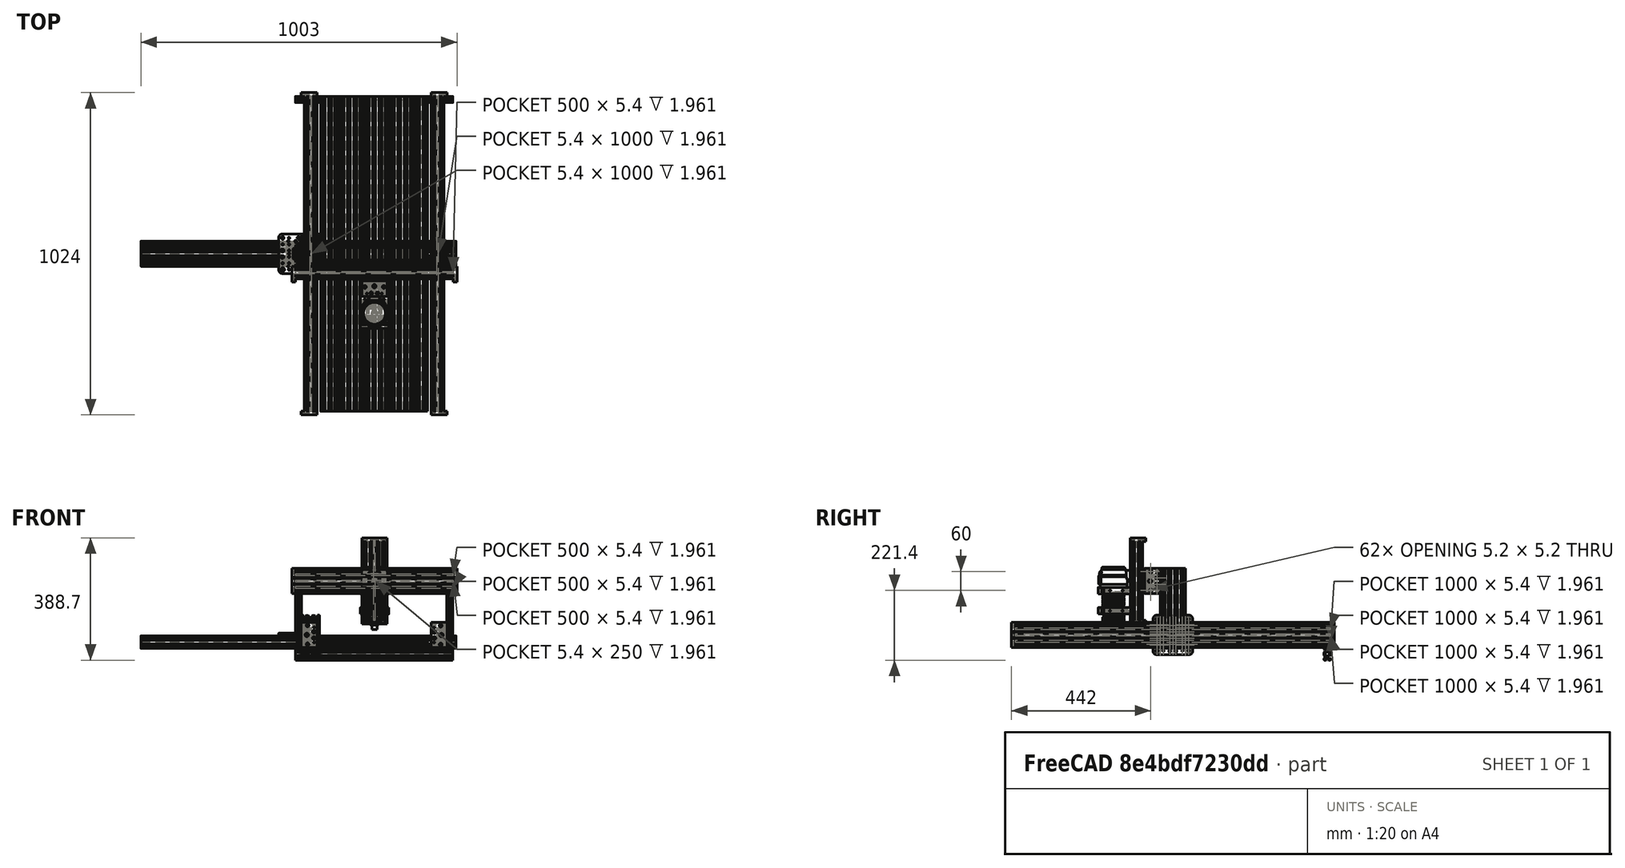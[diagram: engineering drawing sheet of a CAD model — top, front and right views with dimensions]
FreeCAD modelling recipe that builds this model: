
FCSTD DOCUMENT  (FreeCAD 0.19R24276 (Git))
Label: cnc
License: All rights reserved
LicenseURL: http://en.wikipedia.org/wiki/All_rights_reserved
objects: Part::Feature×44, PartDesign::FeatureBase×17, PartDesign::Body×17, Part::MultiFuse×7, App::DocumentObjectGroup×7, Part::Refine×1
note: 86 computed .brp shape members not serialized (recipe doc carries the construction recipe); baked Part::Feature solids carry a one-line shape summary decoded from their .brp

FEATURE [Part::Feature] Part__Feature011  label="Router Spindle Mount"
  Placement = pos=(241,-189,131) rot=(1,0,0;1.5708rad)
  shape: bbox 90.8 x 102.7 x 20 mm, 224 faces, 2 solids (baked)
FEATURE [Part::Feature] Part__Feature012  label="Dewalt DWP611"
  Placement = pos=(241,-189,38) rot=(1,0,0;1.5708rad)
  shape: bbox 86.67 x 107.5 x 199.1 mm, 229 faces (baked)
FEATURE [Part::Feature] Part__Feature013  label="Router Spindle Mount001"
  Placement = pos=(241,-189,66.8) rot=(1,0,0;1.5708rad)
  shape: bbox 90.8 x 102.7 x 20 mm, 224 faces, 2 solids (baked)
FEATURE [Part::Feature] Part__Feature014  label="Frame Front"
  Placement = pos=(-10,-490,-60) rot=(0.57735,0.57735,0.57735;2.0944rad)
  shape: bbox 500 x 20 x 40 mm, 116 faces (baked)
FEATURE [Part::Feature] Part__Feature015  label="V-Slot 20x80x1000 Linear Rail"
  Placement = pos=(250,500,-30) rot=(0.57735,-0.57735,0.57735;2.0944rad)
  shape: bbox 80 x 1000 x 20 mm, 204 faces (baked)
FEATURE [Part::Feature] Part__Feature016  label="V-Slot 20x80x1000 Linear Rail001"
  Placement = pos=(170,500,-30) rot=(0.57735,-0.57735,0.57735;2.0944rad)
  shape: bbox 80 x 1000 x 20 mm, 204 faces (baked)
FEATURE [Part::Feature] Part__Feature017  label="V-Slot 20x80x1000 Linear Rail002"
  Placement = pos=(330,500,-30) rot=(0.57735,-0.57735,0.57735;2.0944rad)
  shape: bbox 80 x 1000 x 20 mm, 204 faces (baked)
FEATURE [Part::Feature] Part__Feature020  label="V-Slot 20x40x1000 Linear Rail"
  Placement = pos=(390,-500,-30) rot=(0.57735,-0.57735,-0.57735;4.18879rad)
  shape: bbox 40 x 1000 x 20 mm, 116 faces (baked)
FEATURE [Part::Feature] Part__Feature021  label="V-Slot 20x60x1000 Linear Rail"
  Placement = pos=(100,500,-30) rot=(0.57735,-0.57735,0.57735;2.0944rad)
  shape: bbox 60 x 1000 x 20 mm, 160 faces (baked)
FEATURE [Part::Refine] Part__Feature014001  label="Frame Back"
  Placement = pos=(0,980,0) rot=(0,0,1;0rad)
  Source = -> Part__Feature014
FEATURE [Part::Feature] Part__Feature014003  label="Xtreme Mini V Wheel"
  shape: bbox 8.8 x 15.23 x 15.23 mm, 16 faces (baked)
FEATURE [Part::Feature] Part__Feature014004  label="Ball Bearing 5 x 10 x 4.2"
  Placement = pos=(2.6,0,0) rot=(0,0,1;0rad)
  shape: bbox 4.2 x 10 x 10 mm, 18 faces (baked)
FEATURE [Part::Feature] Part__Feature014006  label="Precision Shim 8 x 5 x 1"
  Placement = pos=(5.7,0,0) rot=(0,0,1;1.5708rad)
  shape: bbox 1 x 8 x 8 mm, 6 faces (baked)
FEATURE [Part::Feature] Part__Feature014007  label="Ball Bearing 5 x 10 x 4.004"
  Placement = pos=(-2.6,0,0) rot=(0,0,1;0rad)
  shape: bbox 4.2 x 10 x 10 mm, 18 faces (baked)
FEATURE [Part::Feature] Part__Feature014008  label="Precision Shim 8 x 5 x 002"
  Placement = pos=(-4.7,0,0) rot=(0,0,1;1.5708rad)
  shape: bbox 1 x 8 x 8 mm, 6 faces (baked)
FEATURE [Part::Feature] Part__Feature014009  label="Aluminum Spacer 6mm"
  Placement = pos=(5.7,0,0) rot=(0,1,0;1.5708rad)
  shape: bbox 6 x 10 x 10 mm, 14 faces (baked)
FEATURE [Part::MultiFuse] Fusion001003  label="Wheel"
  Shapes = -> [Part__Feature014003,Part__Feature014009,Part__Feature014008,Part__Feature014007,Part__Feature014006,Part__Feature014004]
FEATURE [Part::Feature] Part__Feature014010  label="C-Beam Gantry Plate"
  shape: bbox 77.15 x 6 x 77.15 mm, 93 faces (baked)
FEATURE [PartDesign::FeatureBase] Clone
  BaseFeature = -> Fusion001003
FEATURE [PartDesign::Body] Body  label="Wheel1"
  BaseFeature = -> Fusion001003
  Group = -> [Clone]
  Origin = -> Origin
  Placement = pos=(-30,-11.7,14.25) rot=(0,0,1;1.5708rad)
  Tip = -> Clone
FEATURE [PartDesign::FeatureBase] Clone001
  BaseFeature = -> Fusion001003
FEATURE [PartDesign::Body] Body001  label="Wheel2"
  BaseFeature = -> Fusion001003
  Group = -> [Clone001]
  Origin = -> Origin001
  Placement = pos=(30,-11.7,14.25) rot=(0,0,1;1.5708rad)
  Tip = -> Clone001
FEATURE [PartDesign::FeatureBase] Clone002
  BaseFeature = -> Fusion001003
FEATURE [PartDesign::Body] Body002  label="Wheel3"
  BaseFeature = -> Fusion001003
  Group = -> [Clone002]
  Origin = -> Origin002
  Placement = pos=(30,-11.7,-14.25) rot=(0,0,1;1.5708rad)
  Tip = -> Clone002
FEATURE [PartDesign::FeatureBase] Clone003
  BaseFeature = -> Fusion001003
FEATURE [PartDesign::Body] Body003  label="Wheel4"
  BaseFeature = -> Fusion001003
  Group = -> [Clone003]
  Origin = -> Origin003
  Placement = pos=(-30,-11.7,-14.25) rot=(0,0,1;1.5708rad)
  Tip = -> Clone003
FEATURE [Part::MultiFuse] Fusion001004  label="Granty Plate"
  Shapes = -> [Part__Feature014010,Body,Body001,Body002,Body003]
FEATURE [Part::Feature] Part__Feature003001  label="C-Beam 40x80x1000 Linear Rail002"
  Placement = pos=(37.7,500,0.3) rot=(0,0.707107,-0.707107;3.14159rad)
  shape: bbox 40 x 1000 x 80 mm, 294 faces (baked)
FEATURE [Part::Feature] Part__Feature014011  label="C-Beam End Mount1"
  Placement = pos=(57.7,-500,-39.7) rot=(0.57735,-0.57735,0.57735;2.0944rad)
  shape: bbox 50 x 12 x 80 mm, 43 faces (baked)
FEATURE [Part::Feature] Part__Feature014011001  label="C-Beam End Mount2"
  Placement = pos=(57.7,500,40.3) rot=(0.57735,-0.57735,-0.57735;4.18879rad)
  shape: bbox 50 x 12 x 80 mm, 43 faces (baked)
FEATURE [Part::Feature] Part__Feature002001  label="C-Beam 40x80x500 Linear Rail001"
  Placement = pos=(-250,0,0.3) rot=(0.57735,0.57735,0.57735;2.0944rad)
  shape: bbox 500 x 40 x 80 mm, 294 faces (baked)
FEATURE [PartDesign::FeatureBase] Clone008
  BaseFeature = -> Fusion001004
FEATURE [PartDesign::Body] Body008
  BaseFeature = -> Fusion001004
  Group = -> [Clone008]
  Origin = -> Origin008
  Placement = pos=(0,21.7,0) rot=(0,0,1;0rad)
  Tip = -> Clone008
FEATURE [Part::Feature] Part__Feature014011002  label="C-Beam End Mount003"
  Placement = pos=(-250,-20,-39.7) rot=(0,-1,0;1.5708rad)
  shape: bbox 12 x 50 x 80 mm, 43 faces (baked)
FEATURE [Part::Feature] Part__Feature014011002001  label="C-Beam End Mount004"
  Placement = pos=(250,-20,40.3) rot=(0,1,0;1.5708rad)
  shape: bbox 12 x 50 x 80 mm, 43 faces (baked)
FEATURE [Part::MultiFuse] Fusion001006  label="C-Beam 500 Linear Rail"
  Shapes = -> [Part__Feature002001,Body008,Part__Feature014011002,Part__Feature014011002001]
FEATURE [PartDesign::FeatureBase] Clone009
  BaseFeature = -> Fusion001006
FEATURE [PartDesign::Body] Body009  label="x-rail"
  BaseFeature = -> Fusion001006
  Group = -> [Clone009]
  Origin = -> Origin009
  Placement = pos=(241,-60,171.7) rot=(1,0,0;3.14159rad)
  Tip = -> Clone009
FEATURE [App::DocumentObjectGroup] Group003  label="x-axis"
  Group = -> [Body009]
FEATURE [Part::Feature] Part__Feature014011002002  label="C-Beam 40x80x250 Linear Rail001"
  Placement = pos=(0,125,0.3) rot=(0,0.707107,-0.707107;3.14159rad)
  shape: bbox 40 x 250 x 80 mm, 294 faces (baked)
FEATURE [PartDesign::FeatureBase] Clone010
  BaseFeature = -> Fusion001004
FEATURE [PartDesign::Body] Body010
  BaseFeature = -> Fusion001004
  Group = -> [Clone010]
  Origin = -> Origin010
  Placement = pos=(-21.7,0,0) rot=(0,0,1;1.5708rad)
  Tip = -> Clone010
FEATURE [Part::Feature] Part__Feature014011002003  label="C-Beam End Mount005"
  Placement = pos=(20,-125,-39.7) rot=(0.57735,-0.57735,0.57735;2.0944rad)
  shape: bbox 50 x 12 x 80 mm, 43 faces (baked)
FEATURE [Part::Feature] Part__Feature014011001001  label="C-Beam End Mount006"
  Placement = pos=(20,125,40.3) rot=(0.57735,-0.57735,-0.57735;4.18879rad)
  shape: bbox 50 x 12 x 80 mm, 43 faces (baked)
FEATURE [Part::MultiFuse] Fusion  label="C-Beam 250 Linear Rail"
  Shapes = -> [Body010,Part__Feature014011002003,Part__Feature014011001001,Part__Feature014011002002]
FEATURE [PartDesign::FeatureBase] Clone011
  BaseFeature = -> Fusion
FEATURE [PartDesign::Body] Body011  label="z-rail"
  BaseFeature = -> Fusion
  Group = -> [Clone011]
  Origin = -> Origin011
  Placement = pos=(241,-115.4,171.7) rot=(0.57735,-0.57735,-0.57735;2.0944rad)
  Tip = -> Clone011
FEATURE [Part::Feature] Part__Feature  label="y-left"
  Placement = pos=(0,0,-38.6) rot=(0,0,1;0rad)
  shape: bbox 20 x 80 x 250 mm, 200 faces (baked)
FEATURE [Part::Feature] Part__Feature001  label="y-right"
  Placement = pos=(480,0,-38.6) rot=(0,0,1;0rad)
  shape: bbox 20 x 80 x 250 mm, 200 faces (baked)
FEATURE [App::DocumentObjectGroup] Group  label="Frame"
  Group = -> [Part__Feature014,Part__Feature014001]
FEATURE [App::DocumentObjectGroup] Group009  label="z-axis"
  Group = -> [Part__Feature012,Body011,Part__Feature011,Part__Feature013]
FEATURE [App::DocumentObjectGroup] Group010  label="Bed"
  Group = -> [Part__Feature020,Part__Feature016,Part__Feature017,Part__Feature021,Part__Feature015]
FEATURE [Part::Feature] Part__Feature014011002004  label="Solid V Wheel"
  shape: bbox 10.2 x 23.9 x 23.9 mm, 16 faces (baked)
FEATURE [Part::Feature] Part__Feature014011002005  label="Ball Bearing 8 x 16 x 5"
  Placement = pos=(-3,0,0) rot=(0,0,1;0rad)
  shape: bbox 5 x 16 x 16 mm, 18 faces (baked)
FEATURE [Part::Feature] Part__Feature014011002006  label="Ball Bearing 8 x 16 x 006"
  Placement = pos=(3,0,0) rot=(0,0,1;0rad)
  shape: bbox 5 x 16 x 16 mm, 18 faces (baked)
FEATURE [Part::Feature] Part__Feature014011002007  label="Precision Shim 8 x 5 x 003"
  Placement = pos=(0.5,0,0) rot=(0,0,1;1.5708rad)
  shape: bbox 1 x 8 x 8 mm, 6 faces (baked)
FEATURE [Part::Feature] Part__Feature014011002008  label="Precision Shim 8 x 5 x 004"
  Placement = pos=(-5.5,0,0) rot=(0,0,1;1.5708rad)
  shape: bbox 1 x 8 x 8 mm, 6 faces (baked)
FEATURE [Part::Feature] Part__Feature014011002009  label="Aluminum Spacer 6mm001"
  Placement = pos=(-12.5,0,0) rot=(0,1,0;1.5708rad)
  shape: bbox 6 x 10 x 10 mm, 14 faces (baked)
FEATURE [Part::Feature] Part__Feature014011002010  label="C-Beam Gantry Plate XLarge"
  shape: bbox 125 x 125 x 6 mm, 167 faces (baked)
FEATURE [Part::Feature] Part__Feature014011002011  label="C-Beam 40x80x1000 Linear Rail"
  Placement = pos=(500,0,-22.5) rot=(0,-1,0;1.5708rad)
  shape: bbox 1000 x 80 x 40 mm, 294 faces (baked)
FEATURE [Part::Feature] Part__Feature014011002015  label="Ball Bearing 8 x 16 x 007"
  Placement = pos=(17,0,0) rot=(0,0,1;0rad)
  shape: bbox 5 x 16 x 16 mm, 18 faces (baked)
FEATURE [Part::Feature] Part__Feature014011002016  label="Precision Shim 8 x 5 x 007"
  Placement = pos=(20.5,0,0) rot=(0,0,1;1.5708rad)
  shape: bbox 1 x 8 x 8 mm, 6 faces (baked)
FEATURE [Part::Feature] Part__Feature014011002017  label="Ball Bearing 8 x 16 x 008"
  Placement = pos=(23,0,0) rot=(0,0,1;0rad)
  shape: bbox 5 x 16 x 16 mm, 18 faces (baked)
FEATURE [Part::Feature] Part__Feature014011002018  label="Solid V Wheel001"
  Placement = pos=(20,0,0) rot=(0,0,1;0rad)
  shape: bbox 10.2 x 23.9 x 23.9 mm, 16 faces (baked)
FEATURE [Part::Feature] Part__Feature014011002019  label="Aluminum Spacer 9mm"
  Placement = pos=(5.5,0,0) rot=(0,1,0;1.5708rad)
  shape: bbox 9 x 10 x 10 mm, 14 faces (baked)
FEATURE [Part::Feature] Part__Feature014011002020  label="Precision Shim 8 x 5 x 008"
  Placement = pos=(26.5,0,0) rot=(0,0,1;1.5708rad)
  shape: bbox 1 x 8 x 8 mm, 6 faces (baked)
FEATURE [Part::Feature] Part__Feature014011002021  label="Aluminum Spacer 6mm002"
  Placement = pos=(32.5,0,0) rot=(0.707107,0,-0.707107;3.14159rad)
  shape: bbox 6 x 10 x 10 mm, 14 faces (baked)
FEATURE [Part::MultiFuse] Fusion001007  label="Double Wheel"
  Shapes = -> [Part__Feature014011002004,Part__Feature014011002005,Part__Feature014011002006,Part__Feature014011002007,Part__Feature014011002008,Part__Feature014011002009,Part__Feature014011002015,Part__Feature014011002016,Part__Feature014011002017,Part__Feature014011002018,Part__Feature014011002019,Part__Feature014011002020,Part__Feature014011002021]
FEATURE [Part::Feature] Part__Feature014011002022  label="C-Beam Gantry Plate XLarge001"
  shape: bbox 125 x 125 x 6 mm, 167 faces (baked)
FEATURE [PartDesign::FeatureBase] Clone012
  BaseFeature = -> Fusion001007
FEATURE [PartDesign::Body] Body012
  BaseFeature = -> Fusion001007
  Group = -> [Clone012]
  Origin = -> Origin012
  Placement = pos=(50.32,-50.3,-12.5) rot=(0,1,0;1.5708rad)
  Tip = -> Clone012
FEATURE [PartDesign::FeatureBase] Clone013
  BaseFeature = -> Fusion001007
FEATURE [PartDesign::Body] Body013
  BaseFeature = -> Fusion001007
  Group = -> [Clone013]
  Origin = -> Origin013
  Placement = pos=(50.3,50.3,-12.5) rot=(0,1,0;1.5708rad)
  Tip = -> Clone013
FEATURE [PartDesign::FeatureBase] Clone014
  BaseFeature = -> Fusion001007
FEATURE [PartDesign::Body] Body014
  BaseFeature = -> Fusion001007
  Group = -> [Clone014]
  Origin = -> Origin014
  Placement = pos=(-50.3,-50.3,-12.5) rot=(0,1,0;1.5708rad)
  Tip = -> Clone014
FEATURE [PartDesign::FeatureBase] Clone015
  BaseFeature = -> Fusion001007
FEATURE [PartDesign::Body] Body015
  BaseFeature = -> Fusion001007
  Group = -> [Clone015]
  Origin = -> Origin015
  Placement = pos=(-50.3,50.32,-12.5) rot=(0,1,0;1.5708rad)
  Tip = -> Clone015
FEATURE [PartDesign::FeatureBase] Clone016
  BaseFeature = -> Fusion001007
FEATURE [PartDesign::Body] Body016
  BaseFeature = -> Fusion001007
  Group = -> [Clone016]
  Origin = -> Origin016
  Placement = pos=(0,50.3,-12.5) rot=(0,1,0;1.5708rad)
  Tip = -> Clone016
FEATURE [PartDesign::FeatureBase] Clone017
  BaseFeature = -> Fusion001007
FEATURE [PartDesign::Body] Body017
  BaseFeature = -> Fusion001007
  Group = -> [Clone017]
  Origin = -> Origin017
  Placement = pos=(0,-50.3,-12.5) rot=(0,1,0;1.5708rad)
  Tip = -> Clone017
FEATURE [Part::Feature] Part__Feature014011002023  label="C-Beam Gantry Plate XLarge002"
  Placement = pos=(0,0,-51) rot=(0,0,1;0rad)
  shape: bbox 125 x 125 x 6 mm, 167 faces (baked)
FEATURE [Part::MultiFuse] Fusion001008  label="XL Granty Plate"
  Placement = pos=(15,0,0) rot=(0,-1,0;1.5708rad)
  Shapes = -> [Part__Feature014011002022,Body012,Body013,Body014,Body015,Body016,Body017,Part__Feature014011002023]
FEATURE [PartDesign::FeatureBase] Clone018
  BaseFeature = -> Fusion001004
FEATURE [PartDesign::Body] Body018
  Group = -> [Clone018]
  Origin = -> Origin018
  Placement = pos=(16,0,0.5) rot=(0,0,1;1.5708rad)
  Tip = -> Clone018
FEATURE [Part::MultiFuse] Fusion001005  label="C-Beam 1000 Linear Rail"
  Shapes = -> [Part__Feature003001,Part__Feature014011001,Body018,Part__Feature014011]
FEATURE [App::DocumentObjectGroup] Group007  label="Compounds"
  Group = -> [Fusion001003,Fusion001004,Fusion001005,Fusion001006,Fusion,Part__Feature014011002010,Part__Feature014011002011,Fusion001007,Fusion001008]
FEATURE [PartDesign::FeatureBase] Clone006
  BaseFeature = -> Fusion001005
FEATURE [PartDesign::Body] Body006  label="y-left-rail"
  BaseFeature = -> Fusion001005
  Group = -> [Clone006]
  Origin = -> Origin006
  Placement = pos=(1,0,0) rot=(0,0,1;0rad)
  Tip = -> Clone006
FEATURE [PartDesign::FeatureBase] Clone007
  BaseFeature = -> Fusion001005
FEATURE [PartDesign::Body] Body007  label="y-right-rail"
  BaseFeature = -> Fusion001005
  Group = -> [Clone007]
  Origin = -> Origin007
  Placement = pos=(479,0,0) rot=(0,1,0;3.14159rad)
  Tip = -> Clone007
FEATURE [App::DocumentObjectGroup] Group008  label="y-axis"
  Group = -> [Part__Feature,Part__Feature001,Body006,Body007]
FEATURE [App::DocumentObjectGroup] Group005  label="machine"
  Group = -> [Group003,Group,Group008,Group009,Group010]
